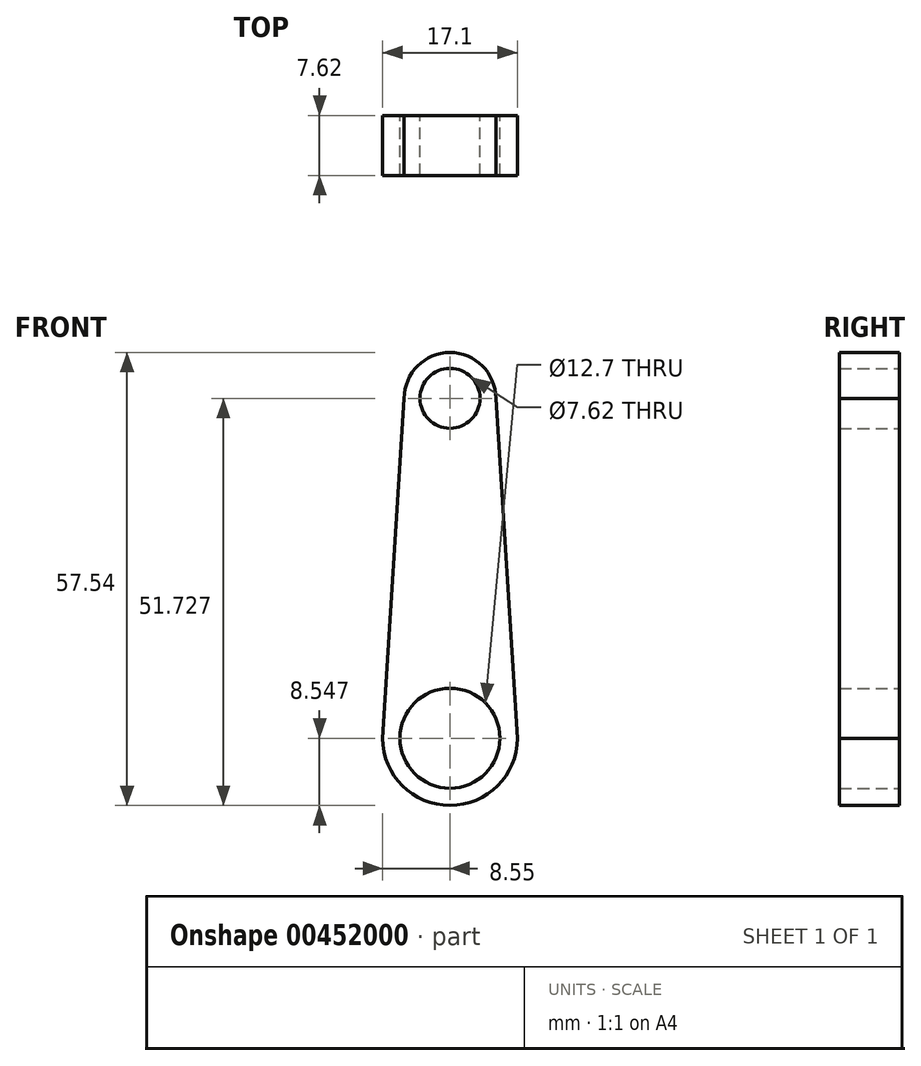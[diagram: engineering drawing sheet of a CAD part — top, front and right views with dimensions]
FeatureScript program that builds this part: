
annotation { "Feature Type Name" : "Feature", "Feature Type Description" : "" }
export const myFeature = defineFeature(function(context is Context, id is Id, definition is map)
    precondition{}
    {
        {
            var Q0;
            Q0=qCreatedBy(makeId("Front.planeOp"),FACE);
            var sketch = newSketch(context, id + "F0", { "sketchPlane" : qUnion([Q0])});
            skCircle(sketch, "E0", {"center": v(0, -17.97) * mm, "radius": 6.35 * mm});
            skCircle(sketch, "E1", {"center": v(0, 25.2) * mm, "radius": 3.81 * mm});
            skArc(sketch, "E2", {"start": v(8.55, -17.97) * mm, "mid": v(0, -26.52) * mm, "end": v(-8.55, -17.97) * mm});
            skArc(sketch, "E3", {"start": v(5.81, 25.2) * mm, "mid": v(0, 31.02) * mm, "end": v(-5.81, 25.2) * mm});
            skLineSegment(sketch, "E4", {"start": v(-5.81, 25.2) * mm, "end": v(-8.55, -17.97) * mm});
            skLineSegment(sketch, "E5", {"start": v(8.55, -17.97) * mm, "end": v(5.81, 25.2) * mm});
            skSolve(sketch);
        }
        {
            var Q0;
            Q0 = qSketchRegion(id + "F0", true);
            extrude(context, id + "F1", {"entities" : qUnion([Q0]), "depth" : 7.62 * mm});
        }
    });
